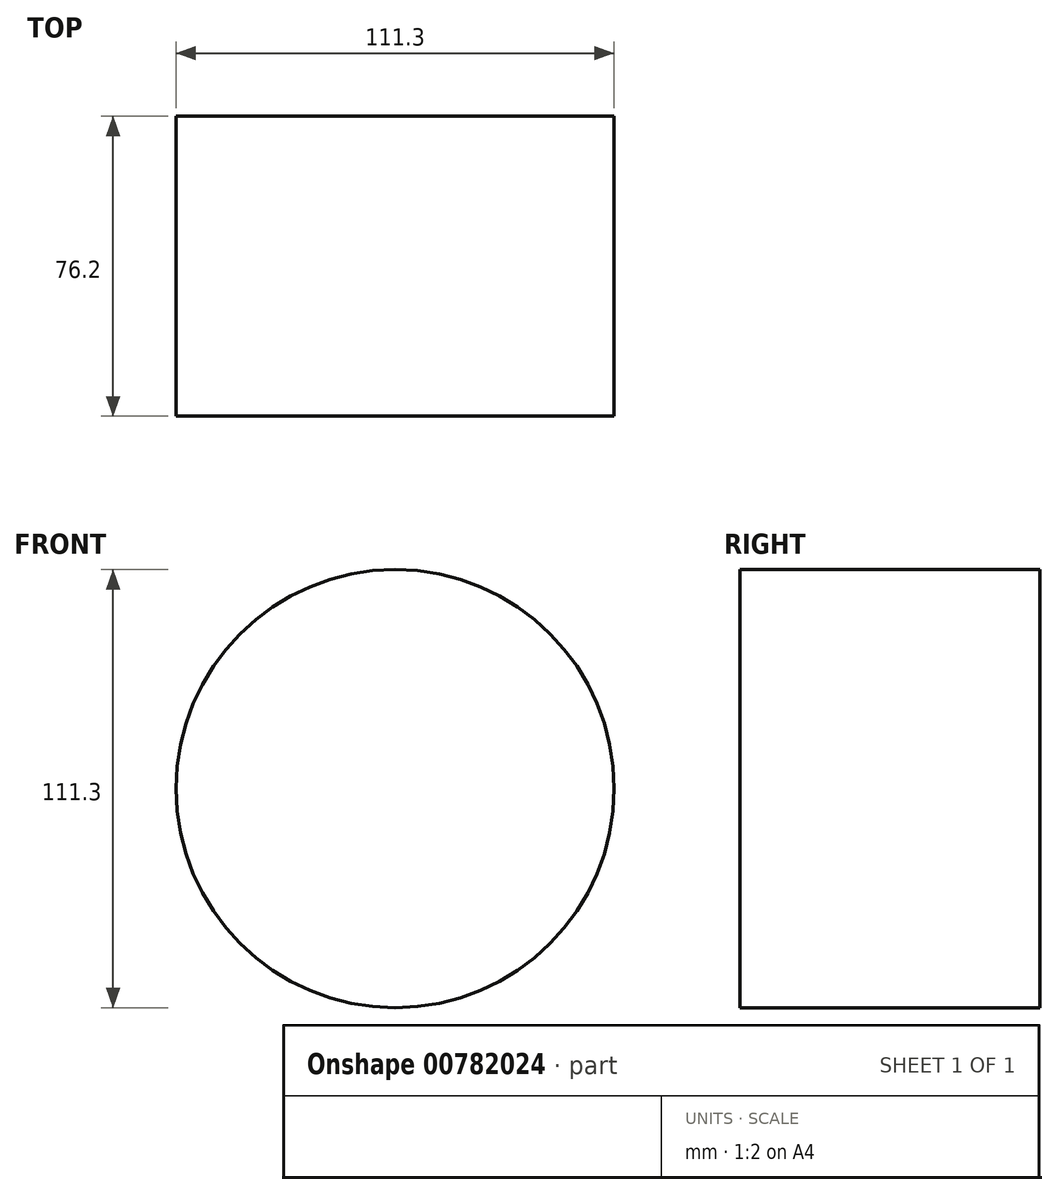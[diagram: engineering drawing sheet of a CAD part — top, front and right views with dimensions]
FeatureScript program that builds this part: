
annotation { "Feature Type Name" : "Feature", "Feature Type Description" : "" }
export const myFeature = defineFeature(function(context is Context, id is Id, definition is map)
    precondition{}
    {
        {
            var Q0;
            Q0=qCreatedBy(makeId("Front.planeOp"),FACE);
            var sketch = newSketch(context, id + "F0", { "sketchPlane" : qUnion([Q0])});
            skCircle(sketch, "E0", {"center": v(0, 0) * mm, "radius": 55.65 * mm});
            skSolve(sketch);
        }
        {
            var Q0;
            Q0=makeQuery(id+"F0.imprint","IMPRINT",FACE,{"disambiguationData":[TD([[makeQuery(id+"F0.imprint","IMPRINT",EDGE,{"derivedFrom":sQuery(id+"F0.wireOp",EDGE,"E0")}),1.0]])]});
            extrude(context, id + "F1", {"entities" : qUnion([Q0]), "oppositeDirection" : true, "depth" : 76.2 * mm, "offsetDistance" : 25.4 * mm});
        }
    });
